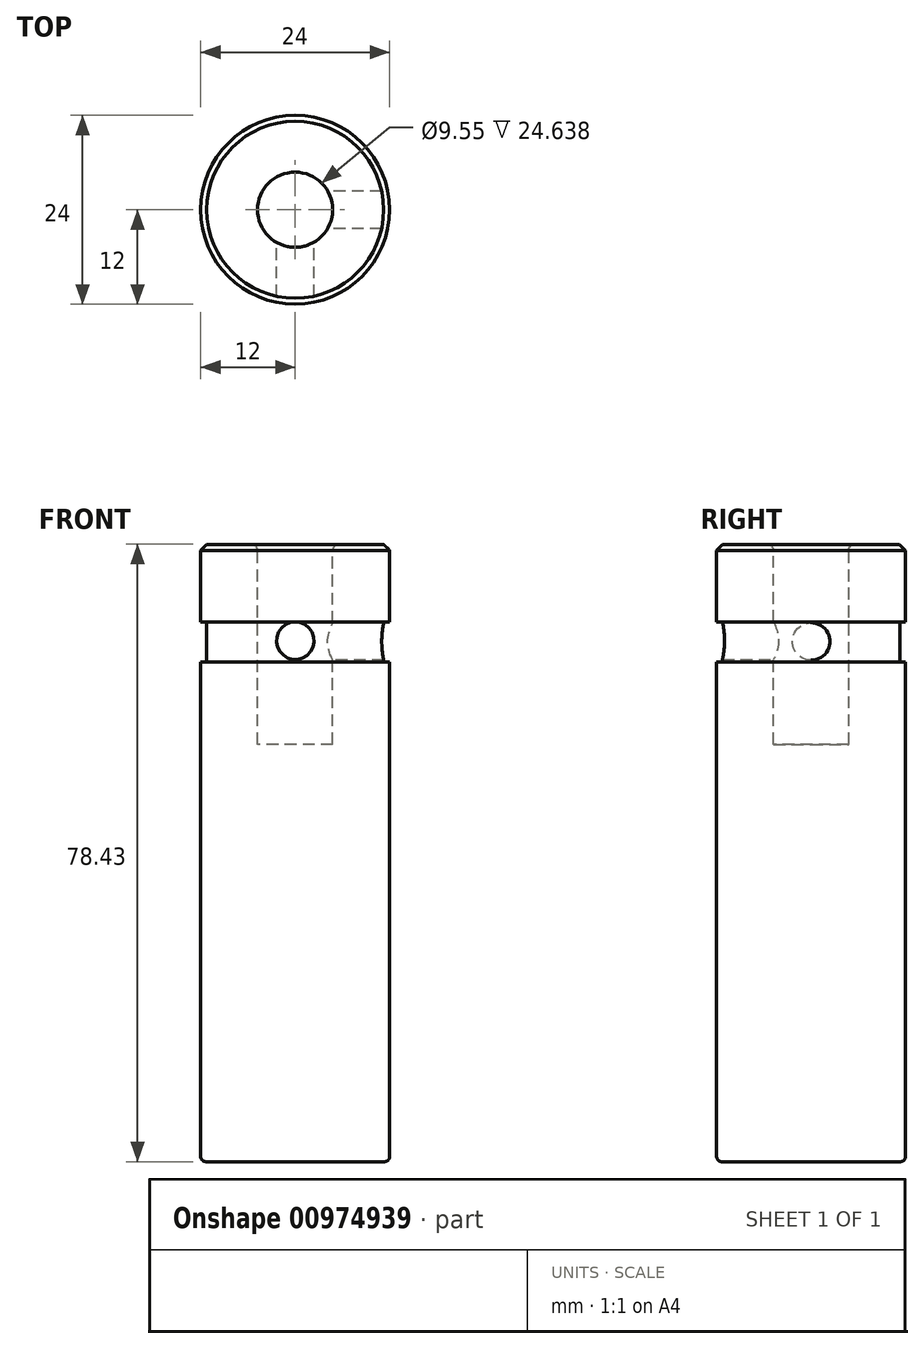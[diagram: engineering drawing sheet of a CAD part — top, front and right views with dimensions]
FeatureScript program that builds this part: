
annotation { "Feature Type Name" : "Feature", "Feature Type Description" : "" }
export const myFeature = defineFeature(function(context is Context, id is Id, definition is map)
    precondition{}
    {
        {
            var Q0;
            Q0=qCreatedBy(makeId("Front.planeOp"),FACE);
            var sketch = newSketch(context, id + "F0", { "sketchPlane" : qUnion([Q0])});
            skLineSegment(sketch, "E0", {"start": v(0, -40.04) * mm, "end": v(11.36, -40.04) * mm});
            skLineSegment(sketch, "E1", {"start": v(12, -39.4) * mm, "end": v(12, 23.46) * mm});
            skLineSegment(sketch, "E2", {"start": v(12, 23.46) * mm, "end": v(11.25, 23.46) * mm});
            skLineSegment(sketch, "E3", {"start": v(11.25, 23.46) * mm, "end": v(11.25, 28.54) * mm});
            skLineSegment(sketch, "E4", {"start": v(11.25, 28.54) * mm, "end": v(12, 28.54) * mm});
            skLineSegment(sketch, "E5", {"start": v(12, 28.54) * mm, "end": v(12, 37.62) * mm});
            skLineSegment(sketch, "E6", {"start": v(11.24, 38.39) * mm, "end": v(5.54, 38.39) * mm});
            skLineSegment(sketch, "E7", {"start": v(4.78, 37.62) * mm, "end": v(4.78, 12.99) * mm});
            skLineSegment(sketch, "E8", {"start": v(4.78, 12.99) * mm, "end": v(0, 12.99) * mm});
            skLineSegment(sketch, "E9", {"start": v(0, 12.99) * mm, "end": v(0, -40.04) * mm});
            skPoint(sketch, "E10.visualSharp", {"position": v(4.78, 38.39) * mm});
            skArc(sketch, "E10.filletArc", {"start": v(5.54, 38.39) * mm, "mid": v(5, 38.16) * mm, "end": v(4.78, 37.62) * mm});
            skPoint(sketch, "E11.visualSharp", {"position": v(12, 38.39) * mm});
            skLineSegment(sketch, "E12", {"start": v(11.24, 38.39) * mm, "end": v(12, 37.62) * mm});
            skPoint(sketch, "E13.visualSharp", {"position": v(12, -40.04) * mm});
            skArc(sketch, "E13.filletArc", {"start": v(11.36, -40.04) * mm, "mid": v(11.81, -39.85) * mm, "end": v(12, -39.4) * mm});
            skSolve(sketch);
        }
        {
            var Q0;
            Q0=makeQuery(id+"F0.imprint","IMPRINT",FACE,{"disambiguationData":[TD([[makeQuery(id+"F0.imprint","IMPRINT",EDGE,{"derivedFrom":sQuery(id+"F0.wireOp",EDGE,"E0")}),1.0]])]});
            var Q1;
            Q1=sQuery(id+"F0.wireOp",EDGE,"E9");
            revolve(context, id + "F1", {"surfaceOperationType" : NewSurfaceOperationType.NEW, "entities" : qUnion([Q0]), "axis" : qUnion([Q1]), "revolveType" : RevolveType.FULL});
        }
        {
            var Q0;
            Q0=qCreatedBy(makeId("Front.planeOp"),FACE);
            var sketch = newSketch(context, id + "F2", { "sketchPlane" : qUnion([Q0])});
            skCircle(sketch, "E14", {"center": v(0, 26.14) * mm, "radius": 2.38 * mm});
            skSolve(sketch);
        }
        {
            var Q0;
            Q0 = qSketchRegion(id + "F2", true);
            extrude(context, id + "F3", {"entities" : qUnion([Q0]), "operationType" : NewBodyOperationType.REMOVE, "depth" : 25.4 * mm, "offsetDistance" : 25.4 * mm});
        }
        {
            var Q0;
            Q0=qCreatedBy(makeId("Right.planeOp"),FACE);
            var sketch = newSketch(context, id + "F4", { "sketchPlane" : qUnion([Q0])});
            skCircle(sketch, "E15", {"center": v(0, 26.04) * mm, "radius": 2.38 * mm});
            skSolve(sketch);
        }
        {
            var Q0;
            Q0 = qSketchRegion(id + "F4", true);
            extrude(context, id + "F5", {"entities" : qUnion([Q0]), "operationType" : NewBodyOperationType.REMOVE, "depth" : 25.4 * mm, "offsetDistance" : 25.4 * mm});
        }
    });
